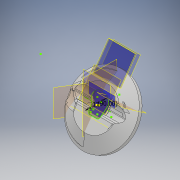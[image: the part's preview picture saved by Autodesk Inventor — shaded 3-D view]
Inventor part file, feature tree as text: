
AUTODESK INVENTOR PART (.ipt)
format: ipt  version: 2018 (Build 220112000, 112)  size: 2,876,928 bytes
history: native  units: mm
features: sketch x125, extrude x113, fillet x31, plane x12, revolve x2, hole x1, direct_edit x1, other x1
ambient origin geometry x8: Origin, YZ Plane, XZ Plane, XY Plane, X Axis, Y Axis, Z Axis, Center Point
bodies: Body1 (feature_tree)
feature tree (286):
  plane  "Work Plane5"
  sketch  "Sketch28"  dims[d118=18.7mm d119=0.0mm d120=0.9mm d121=0.0mm]
  extrude  "Extrusion21"  Depth=0.9mm TaperAngle=0.0deg
  plane  "Work Plane4"
  extrude  "Extrusion22"  Depth=3.8mm
  extrude  "Extrusion23"  Depth=46.7mm
  plane  "Work Plane3"
  hole  "Hole6"  [1 undecoded]
  extrude  "Extrusion27"  Depth=3.8mm
  extrude  "Extrusion28"  Depth=32.03mm
  extrude  "Extrusion30"  Depth=10.0mm TaperAngle=0.0deg
  extrude  "Extrusion31"  Depth=16.3mm TaperAngle=0.0deg
  sketch  "Sketch56"  dims[d188=16.3mm d189=0.0mm d190=16.3mm d191=0.0mm]
  sketch  "Sketch57"  dims[d192=16.3mm d193=0.0mm d194=16.3mm d195=0.0mm]
  extrude  "Extrusion33"  Depth=16.3mm TaperAngle=0.0deg
  extrude  "Extrusion34"  Depth=16.3mm TaperAngle=0.0deg
  extrude  "Extrusion35"  Depth=15.9mm TaperAngle=0.0deg
  extrude  "Extrusion36"  Depth=15.9mm TaperAngle=0.0deg
  extrude  "Extrusion37"  TaperAngle=90.0deg  [1 undecoded]
  extrude  "Extrusion38"  TaperAngle=0.0deg  [1 undecoded]
  extrude  "Extrusion39"  Depth=0.2mm TaperAngle=0.0deg
  extrude  "Extrusion40"  Depth=3.17mm
  extrude  "Extrusion41"  Depth=6.1mm
  sketch  "Sketch68"  dims[d251=10.0mm d252=0.0mm d253=3.91mm d254=0.0mm]
  sketch  "Sketch69"  dims[d255=0.0mm d256=0.0mm d257=3.91mm d258=0.0mm]
  extrude  "Extrusion42"  Depth=0.8mm TaperAngle=0.0deg
  extrude  "Extrusion43"  TaperAngle=0.0deg  [1 undecoded]
  extrude  "Extrusion45"  Depth=10.0mm TaperAngle=0.0deg
  extrude  "Extrusion47"  Depth=3.91mm TaperAngle=0.0deg
  extrude  "Extrusion48"  Depth=0.6mm TaperAngle=0.0deg
  extrude  "Extrusion49"  Depth=0.199mm
  direct_edit  "Direct Edit3"
  extrude  "Extrusion51"  TaperAngle=0.0deg  [1 undecoded]
  extrude  "Extrusion52"  Depth=0.7mm TaperAngle=0.0deg
  extrude  "Extrusion53"  Depth=0.09mm TaperAngle=0.0deg
  extrude  "Extrusion54"  TaperAngle=0.0deg  [1 undecoded]
  extrude  "Extrusion55"  Depth=3.9mm TaperAngle=0.0deg
  extrude  "Extrusion60"  TaperAngle=0.0deg  [1 undecoded]
  extrude  "Extrusion61"  Depth=0.657mm
  extrude  "Extrusion62"  Depth=10.0mm TaperAngle=0.0deg
  fillet  "Fillet13"  Radius=10.0mm
  extrude  "Extrusion64"  TaperAngle=0.0deg  [1 undecoded]
  extrude  "Extrusion65"  TaperAngle=0.0deg  [1 undecoded]
  extrude  "Extrusion66"  Depth=0.253mm
  extrude  "Extrusion67"  TaperAngle=0.0deg  [1 undecoded]
  fillet  "Fillet14"  [1 undecoded]
  extrude  "Extrusion68"  Depth=15.0mm
  extrude  "Extrusion69"  Depth=22.68928mm
  extrude  "Extrusion70"  TaperAngle=90.0deg  [1 undecoded]
  fillet  "Fillet15"  [1 undecoded]
  extrude  "Extrusion71"  TaperAngle=90.0deg  [1 undecoded]
  extrude  "Extrusion72"  Depth=3.490659mm
  extrude  "Extrusion73"  Depth=2.0mm TaperAngle=0.0deg
  extrude  "Extrusion74"  TaperAngle=0.0deg  [1 undecoded]
  fillet  "Fillet16"  Radius=10.0mm
  fillet  "Fillet17"  Radius=0.22mm
  extrude  "Extrusion75"  Depth=5.0mm TaperAngle=0.0deg
  plane  "Work Plane6"
  extrude  "Extrusion78"  Depth=10.0mm TaperAngle=0.0deg
  extrude  "Extrusion79"  Depth=10.0mm TaperAngle=0.0deg
  extrude  "Extrusion80"  Depth=10.0mm TaperAngle=0.0deg
  extrude  "Extrusion81"  Depth=10.0mm TaperAngle=0.0deg
  extrude  "Extrusion82"  Depth=10.0mm
  fillet  "Fillet18"  [1 undecoded]
  fillet  "Fillet19"  Radius=5.99mm
  fillet  "Fillet20"  Radius=1.49mm
  extrude  "Extrusion83"  Depth=1.77mm
  extrude  "Extrusion84"  Depth=10.0mm TaperAngle=0.0deg
  fillet  "Fillet21"  Radius=4.0mm
  extrude  "Extrusion87"  Depth=4.0mm TaperAngle=0.0deg
  plane  "Work Plane7"
  extrude  "Extrusion88"  TaperAngle=0.0deg  [1 undecoded]
  extrude  "Extrusion89"  Depth=7.0mm TaperAngle=0.0deg
  extrude  "Extrusion90"  Depth=10.0mm TaperAngle=0.0deg
  extrude  "Extrusion91"  Depth=7.0mm TaperAngle=0.0deg
  fillet  "Fillet27"  Radius=7.0mm
  extrude  "Extrusion93"  Depth=7.0mm TaperAngle=0.0deg
  extrude  "Extrusion94"  Depth=1.7mm TaperAngle=0.0deg
  fillet  "Fillet29"  [1 undecoded]
  extrude  "Extrusion95"  Depth=10.0mm TaperAngle=0.0deg
  extrude  "Extrusion97"  Depth=10.0mm TaperAngle=0.0deg
  extrude  "Extrusion98"  Depth=1.0mm TaperAngle=0.0deg
  extrude  "Extrusion99"  Depth=15.687mm
  extrude  "Extrusion100"  Depth=9.4mm
  extrude  "Extrusion101"  TaperAngle=90.0deg  [1 undecoded]
  extrude  "Extrusion102"  Depth=10.0mm TaperAngle=0.0deg
  extrude  "Extrusion104"  Depth=50.0mm TaperAngle=0.0deg
  fillet  "Fillet30"  Radius=50.0mm
  extrude  "Extrusion106"  Depth=10.0mm TaperAngle=0.0deg
  fillet  "Fillet33"  Radius=32.0mm
  fillet  "Fillet34"  Radius=9.4mm
  fillet  "Fillet35"  [1 undecoded]
  fillet  "Fillet38"  Radius=10.0mm
  extrude  "Extrusion108"  Depth=10.0mm TaperAngle=0.0deg
  extrude  "Extrusion109"  Depth=10.0mm TaperAngle=0.0deg
  extrude  "Extrusion110"  TaperAngle=0.0deg  [1 undecoded]
  extrude  "Extrusion111"  Depth=18.0mm TaperAngle=0.0deg
  extrude  "Extrusion112"  Depth=2.0mm
  sketch  "Sketch146"  dims[d571=2.0mm d572=2.0mm]
  extrude  "Extrusion113"  Depth=2.0mm
  extrude  "Extrusion114"  Depth=2.0mm
  extrude  "Extrusion115"  Depth=2.0mm
  extrude  "Extrusion116"  Depth=2.0mm
  extrude  "Extrusion118"  Depth=2.0mm
  sketch  "Sketch154"  dims[d590=2.0mm d591=4.0mm]
  extrude  "Extrusion119"  Depth=2.0mm
  extrude  "Extrusion120"  Depth=0.7mm TaperAngle=0.0deg
  extrude  "Extrusion121"  Depth=10.0mm TaperAngle=0.0deg
  extrude  "Extrusion122"  Depth=17.0mm TaperAngle=0.0deg
  extrude  "Extrusion123"  Depth=4.0mm
  extrude  "Extrusion124"  Depth=3.0mm
  extrude  "Extrusion125"  [1 undecoded]
  extrude  "Extrusion126"  [1 undecoded]
  extrude  "Extrusion128"  [1 undecoded]
  extrude  "Extrusion129"  [1 undecoded]
  extrude  "Extrusion130"  [1 undecoded]
  plane  "Work Plane9"
  extrude  "Extrusion133"  [1 undecoded]
  extrude  "Extrusion134"  [1 undecoded]
  plane  "Work Plane8"
  extrude  "Extrusion135"  [1 undecoded]
  plane  "Work Plane2"
  revolve  "Revolution3"  [1 undecoded]
  plane  "Work Plane10"
  extrude  "Extrusion136"  [1 undecoded]
  extrude  "Extrusion137"  [1 undecoded]
  extrude  "Extrusion138"  [1 undecoded]
  extrude  "Extrusion139"  [1 undecoded]
  sketch  "Sketch184"
  plane  "Work Plane11"
  extrude  "Extrusion140"  [1 undecoded]
  extrude  "Extrusion141"  [1 undecoded]
  extrude  "Extrusion142"  [1 undecoded]
  extrude  "Extrusion143"  [1 undecoded]
  revolve  "Revolution4"  [1 undecoded]
  extrude  "Extrusion145"  [1 undecoded]
  sketch  "Sketch192"
  extrude  "Extrusion147"  [1 undecoded]
  extrude  "Extrusion148"  [1 undecoded]
  extrude  "Extrusion149"  [1 undecoded]
  sketch  "Sketch198"
  sketch  "Sketch199"
  sketch  "Sketch200"
  extrude  "Extrusion150"  [1 undecoded]
  sketch  "Sketch201"
  sketch  "Sketch202"
  extrude  "Extrusion151"  [1 undecoded]
  extrude  "Extrusion152"  [1 undecoded]
  extrude  "Extrusion153"  [1 undecoded]
  extrude  "Extrusion154"  [1 undecoded]
  sketch  "Sketch207"
  extrude  "Extrusion155"  [1 undecoded]
  fillet  "Fillet39"  [1 undecoded]
  fillet  "Fillet40"  [1 undecoded]
  fillet  "Fillet41"  [1 undecoded]
  fillet  "Fillet42"  [1 undecoded]
  fillet  "Fillet43"  [1 undecoded]
  fillet  "Fillet44"  [1 undecoded]
  fillet  "Fillet45"  [1 undecoded]
  fillet  "Fillet46"  [1 undecoded]
  fillet  "Fillet47"  [1 undecoded]
  plane  "Work Plane12"
  extrude  "Extrusion156"  [1 undecoded]
  fillet  "Fillet48"  [1 undecoded]
  fillet  "Fillet49"  [1 undecoded]
  fillet  "Fillet50"  [1 undecoded]
  fillet  "Fillet51"  [1 undecoded]
  extrude  "Extrusion157"  [1 undecoded]
  fillet  "Fillet52"  [1 undecoded]
  extrude  "Extrusion158"  [1 undecoded]
  extrude  "Extrusion159"  [1 undecoded]
  extrude  "Extrusion161"  [1 undecoded]
  fillet  "Fillet53"  [1 undecoded]
  plane  "Work Plane13"
  extrude  "Extrusion163"  [1 undecoded]
  sketch  "Sketch41"  dims[d122=0.7mm d123=0.0mm d128=3.8mm]
  sketch  "Sketch42"  dims[d129=3.8mm d130=46.7mm]
  sketch  "Sketch43"  dims[d134=3.8mm d135=4.369mm d136=5.824mm d137=2.0mm d138=14.3117mm d139=6.637mm d140=0.0mm d150=1.5mm d151=0.0mm]
  sketch  "Sketch50"  dims[d152=1.2mm d153=0.0mm d159=3.8mm]
  sketch  "Sketch51"  dims[d161=3.8mm d168=23.3333mm d173=32.03mm]
  sketch  "Sketch53"  dims[d174=16.015mm d175=10.0mm d176=0.0mm]
  sketch  "Sketch54"  dims[d179=0.0mm d180=0.0mm d186=16.3mm d187=0.0mm]
  sketch  "Sketch58"  dims[d196=15.9mm d197=0.0mm d198=15.9mm d199=0.0mm]
  sketch  "Sketch60"  dims[d200=15.9mm d201=0.0mm d202=15.9mm d203=0.0mm]
  sketch  "Sketch61"  dims[d209=17.0mm d210=90.0deg]
  sketch  "Sketch62"  dims[d211=6.0mm d212=0.0mm d213=0.0mm d214=0.0mm]
  sketch  "Sketch63"  dims[d225=6.0mm d226=0.0mm d230=0.2mm d231=0.0mm]
  sketch  "Sketch64"  dims[d232=3.17mm d233=3.17mm]
  sketch  "Sketch65"  dims[d235=19.4mm d236=6.1mm]
  sketch  "Sketch66"  dims[d237=0.8mm d238=0.0mm d239=0.8mm d240=0.0mm]
  sketch  "Sketch67"  dims[d246=9.0mm d247=10.0mm d248=10.0mm d249=0.0mm d250=0.0mm]
  sketch  "Sketch70"  dims[d267=0.0mm d268=0.0mm d269=0.6mm d270=0.0mm]
  sketch  "Sketch72"  dims[d271=0.0mm d272=0.0mm d273=0.199mm]
  sketch  "Sketch74"  dims[d276=0.0mm d277=0.0mm d278=0.0mm d279=0.0mm]
  sketch  "Sketch75"  dims[d280=0.7mm d281=0.0mm d282=0.7mm d283=0.0mm]
  sketch  "Sketch76"  dims[d284=3.64mm d285=0.09mm d286=0.0mm]
  sketch  "Sketch79"  dims[d287=0.09mm d288=0.0mm d289=0.0mm d290=0.0mm]
  sketch  "Sketch80"  dims[d291=0.356mm d292=3.9mm d293=0.0mm]
  sketch  "Sketch81"  dims[d294=3.9mm d295=0.0mm d296=0.0mm d297=0.0mm]
  sketch  "Sketch82"  dims[d298=3.9mm d299=0.0mm d300=0.657mm]
  sketch  "Sketch83"  dims[d301=0.886mm d302=3.9mm d303=0.0mm d313=10.0mm d314=0.0mm]
  sketch  "Sketch89"  dims[d315=10.0mm d316=0.0mm d317=0.0mm d318=0.0mm]
  sketch  "Sketch90"  dims[d319=10.0mm d320=0.0mm d321=0.0mm d322=0.0mm]
  sketch  "Sketch91"  dims[d323=0.467mm d324=0.253mm]
  sketch  "Sketch93"  dims[d325=0.195mm d326=0.0mm d327=0.0mm d328=90.0deg]
  sketch  "Sketch94"  dims[d329=90.0deg d330=15.0mm]
  sketch  "Sketch95"  dims[d332=11.0mm d333=22.68928mm]
  sketch  "Sketch96"  dims[d335=90.0deg d336=90.0deg d337=0.0mm d338=0.0mm]
  sketch  "Sketch97"  dims[d344=0.954mm d350=90.0deg]
  sketch  "Sketch98"  dims[d351=3.490659mm d352=3.490659mm]
  sketch  "Sketch99"  dims[d353=6.0mm d354=0.0mm d363=2.0mm d364=0.0mm]
  sketch  "Sketch100"  dims[d365=2.0mm d366=0.0mm d374=0.0mm d375=0.0mm d376=10.0mm d377=0.0mm d378=0.22mm]
  sketch  "Sketch101"  dims[d381=5.0mm d382=0.0mm d383=5.0mm d384=0.0mm]
  sketch  "Sketch102"  dims[d386=3.8mm d397=10.0mm d398=0.0mm]
  sketch  "Sketch103"  dims[d401=0.3mm d402=0.0mm d403=10.0mm d404=0.0mm]
  sketch  "Sketch104"  dims[d405=10.0mm d406=0.0mm d407=10.0mm d408=0.0mm]
  sketch  "Sketch106"  dims[d409=10.0mm d410=0.0mm d411=10.0mm d412=0.0mm]
  sketch  "Sketch107"  dims[d415=10.0mm d416=0.0mm d419=0.865mm d421=0.0mm d422=0.0mm d424=5.99mm d425=1.49mm]
  sketch  "Sketch108"  dims[d426=0.859mm d431=1.77mm]
  sketch  "Sketch109"  dims[d432=10.0mm d433=0.0mm d434=4.0mm d435=0.0mm d436=4.0mm d437=0.0mm]
  sketch  "Sketch110"  dims[d438=4.0mm d439=0.0mm d440=4.0mm d441=0.0mm]
  sketch  "Sketch113"  dims[d442=0.0mm d443=0.0mm d444=0.0mm d445=0.0mm]
  sketch  "Sketch114"  dims[d446=1.0mm d447=0.0mm d448=7.0mm d449=0.0mm]
  sketch  "Sketch117"  dims[d452=7.0mm d453=0.0mm d454=10.0mm d455=0.0mm]
  sketch  "Sketch118"  dims[d456=0.0mm d457=0.0mm d458=7.0mm d459=0.0mm d460=7.0mm d461=0.0mm]
  sketch  "Sketch119"  dims[d462=0.0mm d463=0.0mm d464=7.0mm d465=0.0mm]
  sketch  "Sketch120"  dims[d466=1.7mm d467=0.0mm d468=1.7mm d469=0.0mm d483=0.0mm d484=0.0mm]
  sketch  "Sketch121"  dims[d485=0.0mm d486=0.0mm d487=10.0mm d488=0.0mm]
  sketch  "Sketch123"  dims[d496=10.0mm d497=0.0mm d498=10.0mm d499=0.0mm]
  sketch  "Sketch124"  dims[d500=31.5mm d501=1.0mm d502=0.0mm]
  sketch  "Sketch126"  dims[d508=-1.0mm d509=15.687mm]
  sketch  "Sketch128"  dims[d510=90.0deg d514=9.4mm]
  sketch  "Sketch129"  dims[d516=7.0mm d519=90.0deg]
  sketch  "Sketch130"  dims[d520=2.75mm d521=0.0mm d522=10.0mm d523=0.0mm]
  sketch  "Sketch131"  dims[d524=7.0mm d525=0.0mm d527=50.0mm d528=0.0mm d529=50.0mm d530=0.0mm]
  sketch  "Sketch132"  dims[d531=50.0mm d532=0.0mm d533=50.0mm d534=0.0mm d535=32.0mm d536=0.0mm d537=9.4mm d538=7.0mm d539=90.0deg d542=10.0mm d543=0.0mm]
  sketch  "Sketch133"  dims[d546=10.0mm d547=0.0mm d548=10.0mm d549=0.0mm]
  sketch  "Sketch135"  dims[d550=31.0mm d551=0.0mm d552=10.0mm d553=0.0mm]
  sketch  "Sketch137"  dims[d554=5.5mm d555=0.0mm d556=0.0mm d557=0.0mm]
  sketch  "Sketch141"  dims[d558=5.5mm d559=0.0mm d560=18.0mm d561=0.0mm]
  sketch  "Sketch142"  dims[d562=18.0mm d563=0.0mm d564=2.0mm]
  sketch  "Sketch143"  dims[d565=2.0mm d566=2.0mm]
  sketch  "Sketch144"  dims[d567=2.0mm d568=2.0mm]
  sketch  "Sketch145"  dims[d569=2.0mm d570=2.0mm]
  sketch  "Sketch147"  dims[d573=0.0mm d574=0.0mm d575=2.0mm]
  sketch  "Sketch148"  dims[d576=2.0mm d577=2.0mm]
  sketch  "Sketch149"  dims[d578=2.0mm d579=0.7mm d580=0.0mm]
  sketch  "Sketch150"  dims[d581=2.0mm d582=10.0mm d583=0.0mm]
  sketch  "Sketch153"  dims[d584=2.15mm d585=0.0mm d588=17.0mm d589=0.0mm]
  sketch  "Sketch156"  dims[d594=3.0mm d595=0.0mm d21=1.0mm]
  sketch  "Sketch157"  dims[d22=1.0mm]
  sketch  "Sketch161"
  sketch  "Sketch162"
  sketch  "Sketch163"
  sketch  "Sketch164"
  sketch  "Sketch165"
  sketch  "Sketch166"
  sketch  "Sketch169"
  sketch  "Sketch170"
  sketch  "Sketch171"
  sketch  "Sketch174"
  sketch  "Sketch175"
  sketch  "Sketch176"
  sketch  "Sketch179"
  sketch  "Sketch180"
  sketch  "Sketch181"
  sketch  "Sketch182"
  sketch  "Sketch183"
  sketch  "Sketch185"
  sketch  "Sketch186"
  sketch  "Sketch187"
  sketch  "Sketch188"
  sketch  "Sketch190"
  sketch  "Sketch193"
  sketch  "Sketch194"
  sketch  "Sketch195"
  sketch  "Sketch204"
  sketch  "Sketch205"
  sketch  "Sketch206"
  sketch  "Sketch208"
  sketch  "Sketch209"
  sketch  "Sketch210"
  sketch  "Sketch211"
  sketch  "Sketch212"
  sketch  "Sketch213"
  other  "Scale3"
note: 70 required parameter values undecoded (feature->parameter linkage not recoverable at this tier; creation-order binding heuristic only, values carry confidence <= 0.55)
